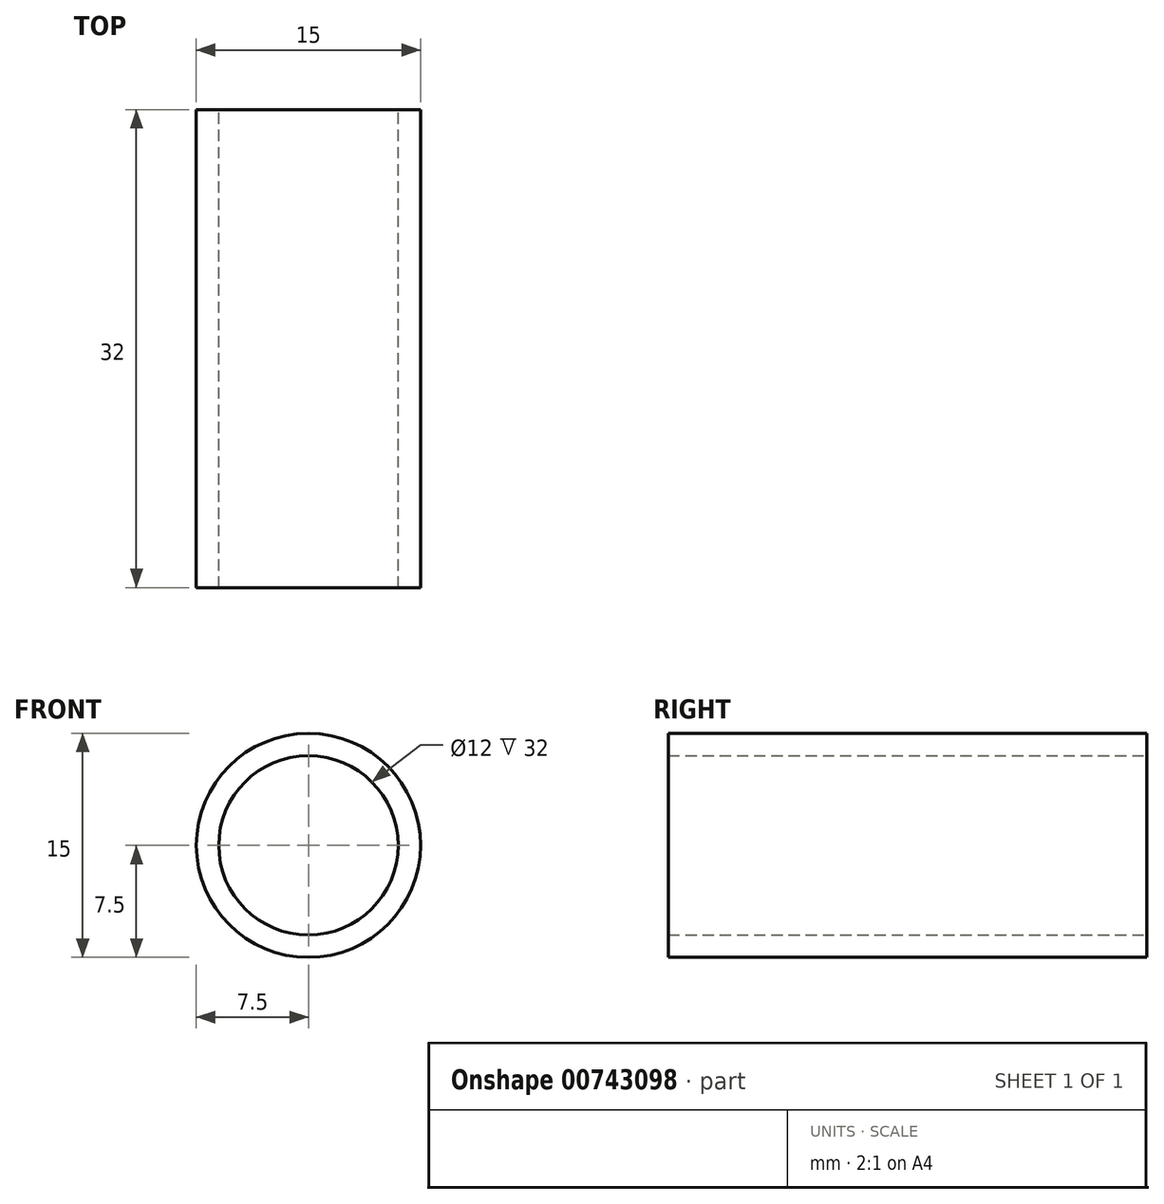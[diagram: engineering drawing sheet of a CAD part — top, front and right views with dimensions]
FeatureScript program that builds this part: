
annotation { "Feature Type Name" : "Feature", "Feature Type Description" : "" }
export const myFeature = defineFeature(function(context is Context, id is Id, definition is map)
    precondition{}
    {
        {
            var Q0;
            Q0=qCreatedBy(makeId("Front.planeOp"),FACE);
            var sketch = newSketch(context, id + "F0", { "sketchPlane" : qUnion([Q0])});
            skCircle(sketch, "E0", {"center": v(0, 0) * mm, "radius": 7.5 * mm});
            skCircle(sketch, "E1", {"center": v(0, 0) * mm, "radius": 6 * mm});
            skSolve(sketch);
        }
        {
            var Q0;
            Q0=qSketchRegion(id+"F0",true);
            extrude(context, id + "F1", {"entities" : qUnion([Q0]), "depth" : 32 * mm, "offsetDistance" : 25 * mm});
        }
    });
